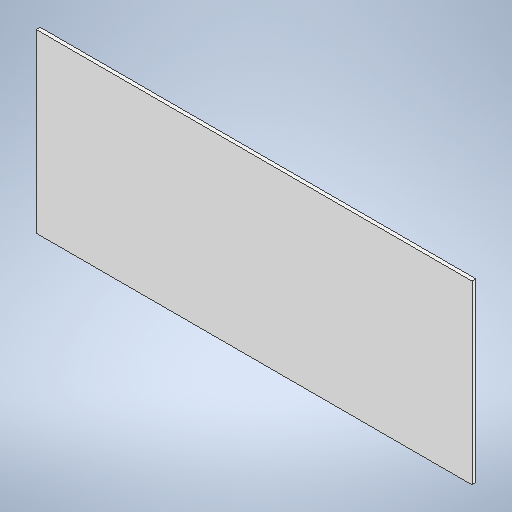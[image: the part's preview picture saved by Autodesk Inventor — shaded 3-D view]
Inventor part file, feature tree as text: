
AUTODESK INVENTOR PART (.ipt)
format: ipt  version: 2025 (Build 290162000, 162)  size: 256,000 bytes
history: native  units: in
note: dims shown in document units (in); Inventor stores cm internally (conversion verified against a paired STEP export)
features: extrude x1, sketch x1
ambient origin geometry x8: Origin, YZ Plane, XZ Plane, XY Plane, X Axis, Y Axis, Z Axis, Center Point
bodies: Solid1 (feature_tree)
feature tree (2):
  extrude  "Extrusion1"  Depth=34.0in
  sketch  "Sketch1"  dims[d1=84.0in d2=34.0in d3=0.75in d4=0.0in]
